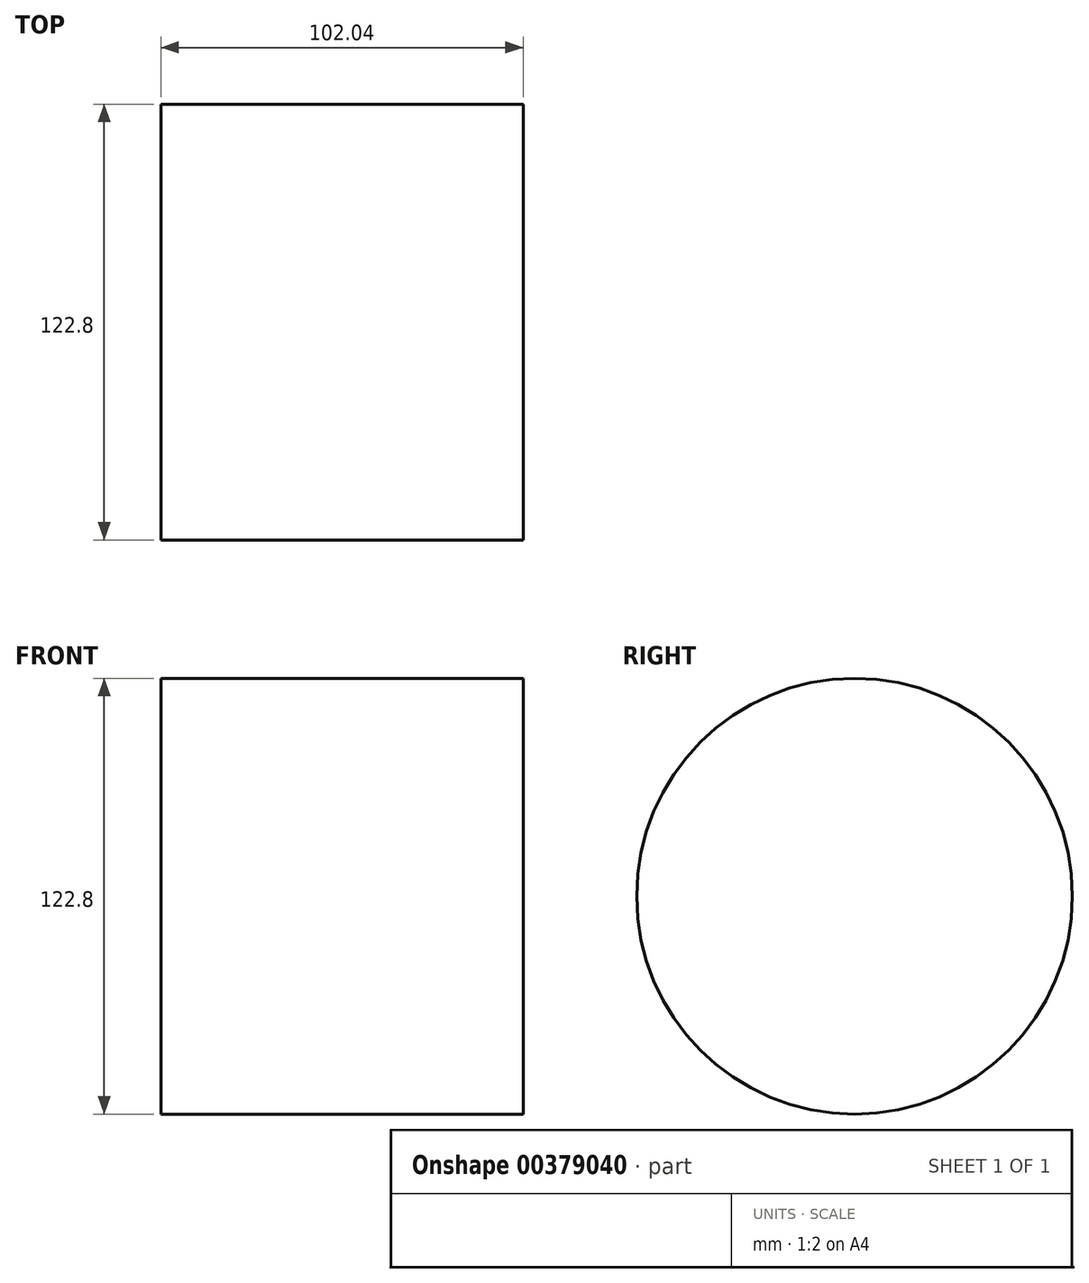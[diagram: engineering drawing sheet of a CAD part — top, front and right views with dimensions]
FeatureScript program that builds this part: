
annotation { "Feature Type Name" : "Feature", "Feature Type Description" : "" }
export const myFeature = defineFeature(function(context is Context, id is Id, definition is map)
    precondition{}
    {
        {
            var Q0;
            Q0=qCreatedBy(makeId("Right.planeOp"),FACE);
            var sketch = newSketch(context, id + "F0", { "sketchPlane" : qUnion([Q0])});
            skCircle(sketch, "E0", {"center": v(0, 0) * mm, "radius": 61.4 * mm});
            skSolve(sketch);
        }
        {
            var Q0;
            Q0 = qSketchRegion(id + "F0", true);
            extrude(context, id + "F1", {"entities" : qUnion([Q0]), "depth" : 102.04 * mm});
        }
    });
